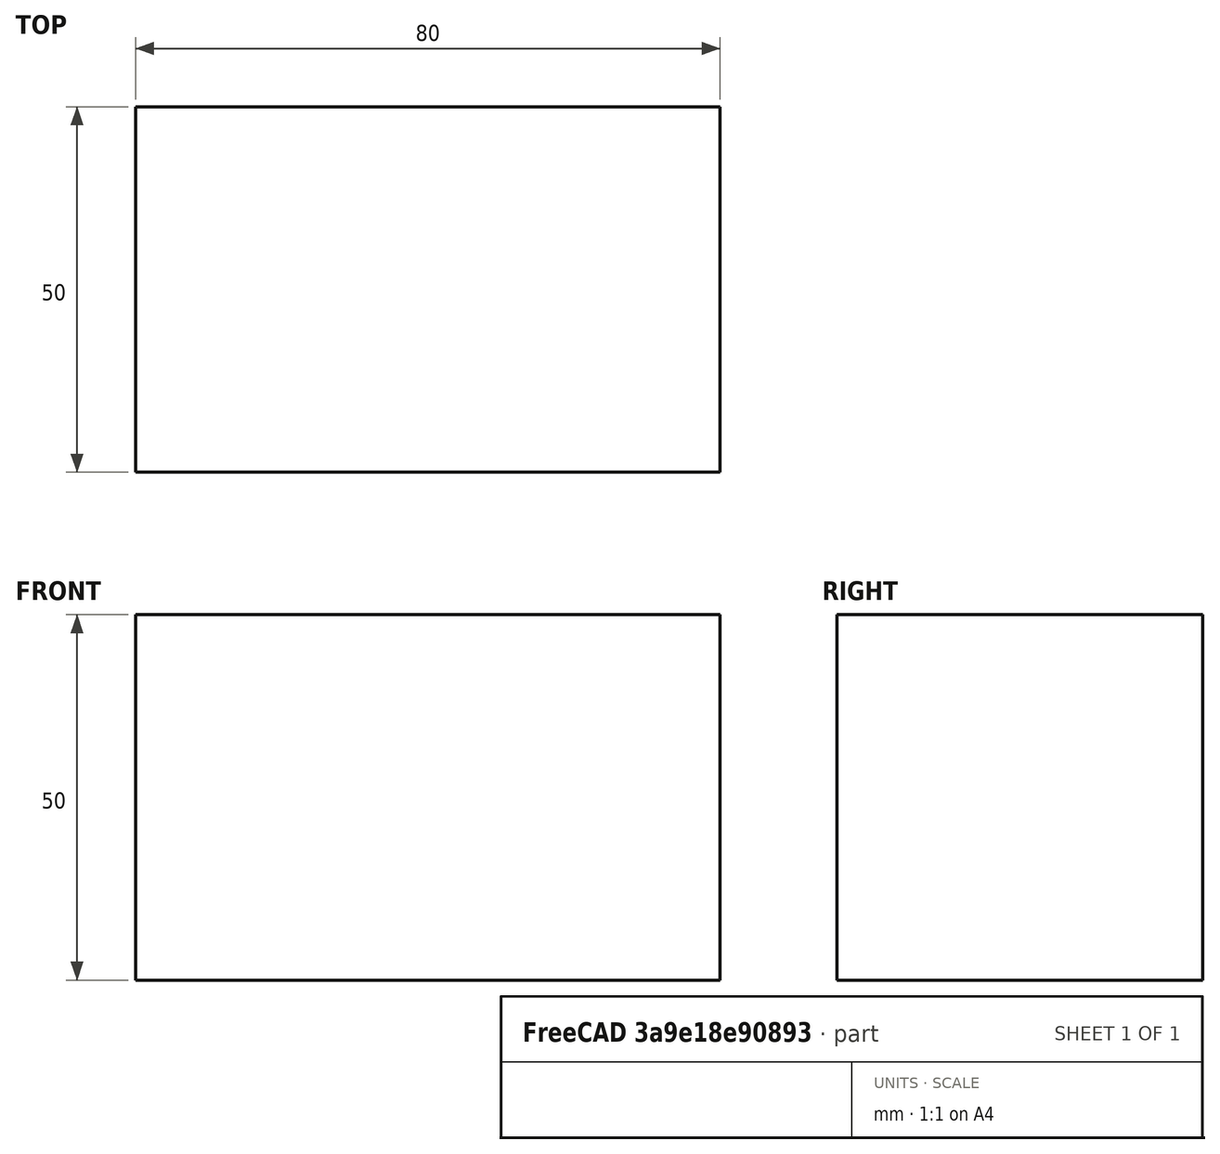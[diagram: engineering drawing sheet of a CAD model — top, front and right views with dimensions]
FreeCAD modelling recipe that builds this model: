
FCSTD DOCUMENT  (FreeCAD 0.15R4671 (Git))
Label: Flat Bar 80x50 EN10058 S235JR
License: All rights reserved
LicenseURL: http://en.wikipedia.org/wiki/All_rights_reserved
objects: Sketcher::SketchObject×1, Part::Extrusion×1
note: 2 computed .brp shape members not serialized (recipe doc carries the construction recipe); baked Part::Feature solids carry a one-line shape summary decoded from their .brp

FEATURE [Sketcher::SketchObject] Sketch
  sketch-geometry (4):
    g0: LineSegment StartX=-40 StartY=-25 StartZ=0 EndX=40 EndY=-25 EndZ=0
    g1: LineSegment StartX=40 StartY=-25 StartZ=0 EndX=40 EndY=25 EndZ=0
    g2: LineSegment StartX=40 StartY=25 StartZ=0 EndX=-40 EndY=25 EndZ=0
    g3: LineSegment StartX=-40 StartY=25 StartZ=0 EndX=-40 EndY=-25 EndZ=0
  constraints (12):
    c: Coincident(g0,g1)
    c: Coincident(g1,g2)
    c: Coincident(g2,g3)
    c: Coincident(g3,g0)
    c: Horizontal(g0)
    c: Horizontal(g2)
    c: Vertical(g1)
    c: Vertical(g3)
    c: Symmetric(g1,g2,g-2)
    c: Symmetric(g0,g1,g-1)
    c: DistanceY(g1) = 50
    c: DistanceX(g0) = 80
FEATURE [Part::Extrusion] Extrude  label="Flat Bar 80x50 EN10058 S235JR"
  Base = -> Sketch
  Dir = (0,0,50)
  Solid = true
